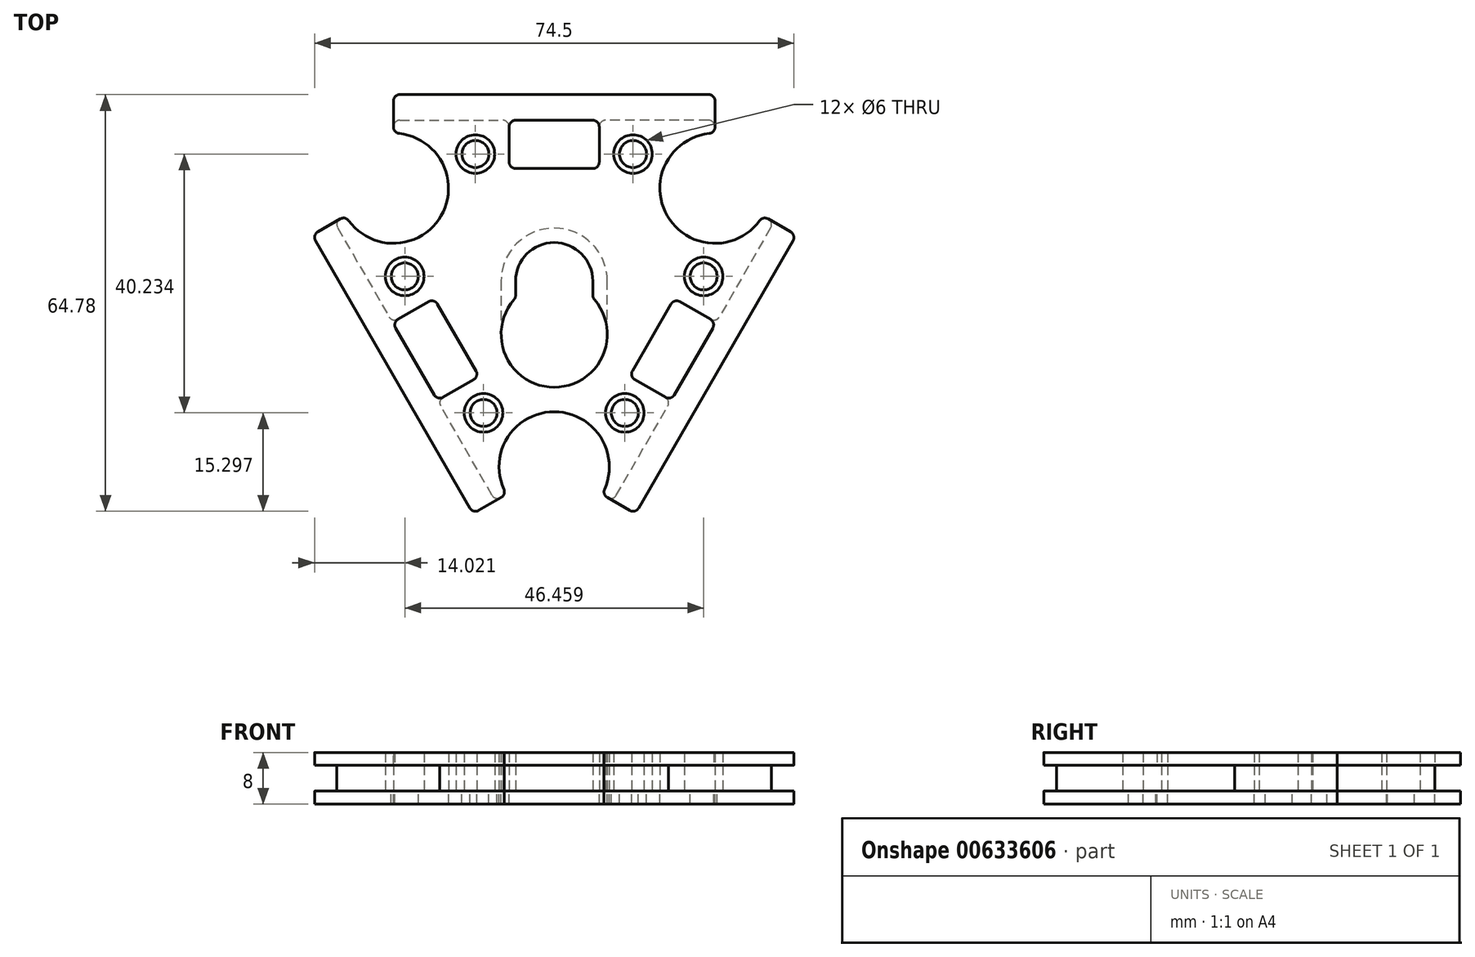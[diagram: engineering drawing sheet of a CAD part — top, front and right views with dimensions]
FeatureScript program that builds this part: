
annotation { "Feature Type Name" : "Feature", "Feature Type Description" : "" }
export const myFeature = defineFeature(function(context is Context, id is Id, definition is map)
    precondition{}
    {
        {
            var Q0;
            Q0=qCreatedBy(makeId("Top.planeOp"),FACE);
            var sketch = newSketch(context, id + "F0", { "sketchPlane" : qUnion([Q0])});
            skLineSegment(sketch, "E0.MirrorCS", {"start": v(-24, 25) * mm, "end": v(-8, 25) * mm});
            skLineSegment(sketch, "E1.MirrorCS", {"start": v(-25, 24) * mm, "end": v(-25, 23.95) * mm});
            skLineSegment(sketch, "E2.1.19", {"start": v(0, 0) * mm, "end": v(-17.58, 10.15) * mm, "construction": true});
            skArc(sketch, "E3", {"start": v(-17.58, 10.15) * mm, "mid": v(-17.37, 18.32) * mm, "end": v(-24.1, 22.95) * mm});
            skLineSegment(sketch, "E4", {"start": v(-25, 23) * mm, "end": v(0, 23) * mm, "construction": true});
            skLineSegment(sketch, "E5.top", {"start": v(0, 17.5) * mm, "end": v(-6, 17.5) * mm});
            skLineSegment(sketch, "E5.right", {"start": v(-7, 24) * mm, "end": v(-7, 18.5) * mm});
            skArc(sketch, "E6", {"start": v(6, 0) * mm, "mid": v(0, 6) * mm, "end": v(-6, 0) * mm});
            skArc(sketch, "E7", {"start": v(-6.24, -2.86) * mm, "mid": v(0, -16.5) * mm, "end": v(6.24, -2.86) * mm});
            skLineSegment(sketch, "E8", {"start": v(0, 27) * mm, "end": v(-25, 27) * mm, "construction": true});
            skCircle(sketch, "E9", {"center": v(-25, 27) * mm, "radius": 2 * mm, "construction": true});
            skLineSegment(sketch, "E10", {"start": v(-17.58, 10.15) * mm, "end": v(-7.85, 27) * mm, "construction": true});
            skLineSegment(sketch, "E11", {"start": v(-6, 0) * mm, "end": v(-6, -2.2) * mm});
            skLineSegment(sketch, "E12", {"start": v(6, -2.2) * mm, "end": v(6, 0) * mm});
            skCircle(sketch, "E13", {"center": v(-12.25, 19.75) * mm, "radius": 3 * mm});
            skCircle(sketch, "E14", {"center": v(-12.25, 19.75) * mm, "radius": 5.25 * mm, "construction": true});
            skPoint(sketch, "E15.visualSharp", {"position": v(-7, 25) * mm});
            skArc(sketch, "E15.filletArc", {"start": v(-7, 24) * mm, "mid": v(-7.3, 24.7) * mm, "end": v(-8, 25) * mm});
            skPoint(sketch, "E16.visualSharp", {"position": v(-25, 25) * mm});
            skArc(sketch, "E16.filletArc", {"start": v(-24, 25) * mm, "mid": v(-24.7, 24.7) * mm, "end": v(-25, 24) * mm});
            skPoint(sketch, "E17.visualSharp", {"position": v(-25, 23) * mm});
            skArc(sketch, "E17.filletArc", {"start": v(-25, 23.95) * mm, "mid": v(-24.74, 23.28) * mm, "end": v(-24.1, 22.95) * mm});
            skPoint(sketch, "E18.visualSharp", {"position": v(-7, 17.5) * mm});
            skArc(sketch, "E18.filletArc", {"start": v(-7, 18.5) * mm, "mid": v(-6.7, 17.8) * mm, "end": v(-6, 17.5) * mm});
            skPoint(sketch, "E19.visualSharp", {"position": v(-6, -2.59) * mm});
            skArc(sketch, "E19.filletArc", {"start": v(-6.24, -2.86) * mm, "mid": v(-6.06, -2.55) * mm, "end": v(-6, -2.2) * mm});
            skPoint(sketch, "E20.visualSharp", {"position": v(6, -2.59) * mm});
            skArc(sketch, "E20.filletArc", {"start": v(6, -2.2) * mm, "mid": v(6.06, -2.55) * mm, "end": v(6.24, -2.86) * mm});
            skLineSegment(sketch, "E21", {"start": v(0, 27) * mm, "end": v(0, 0) * mm, "construction": true});
            skLineSegment(sketch, "E22.MirrorCS", {"start": v(25, 24) * mm, "end": v(25, 23.95) * mm});
            skArc(sketch, "E23.MirrorCS", {"start": v(7, 24) * mm, "mid": v(7.3, 24.7) * mm, "end": v(8, 25) * mm});
            skArc(sketch, "E24.MirrorCS", {"start": v(24, 25) * mm, "mid": v(24.7, 24.7) * mm, "end": v(25, 24) * mm});
            skArc(sketch, "E25.MirrorCS", {"start": v(25, 23.95) * mm, "mid": v(24.74, 23.28) * mm, "end": v(24.1, 22.95) * mm});
            skArc(sketch, "E26.MirrorCS", {"start": v(7, 18.5) * mm, "mid": v(6.7, 17.8) * mm, "end": v(6, 17.5) * mm});
            skLineSegment(sketch, "E27.MirrorCS", {"start": v(25, 23) * mm, "end": v(0, 23) * mm, "construction": true});
            skLineSegment(sketch, "E28.MirrorCS", {"start": v(7, 24) * mm, "end": v(7, 18.5) * mm});
            skArc(sketch, "E29.MirrorCS", {"start": v(17.58, 10.15) * mm, "mid": v(17.37, 18.32) * mm, "end": v(24.1, 22.95) * mm});
            skPoint(sketch, "E30.MirrorP", {"position": v(25, 23) * mm});
            skPoint(sketch, "E31.MirrorP", {"position": v(25, 25) * mm});
            skPoint(sketch, "E32.MirrorP", {"position": v(7, 17.5) * mm});
            skCircle(sketch, "E33.MirrorC", {"center": v(12.25, 19.75) * mm, "radius": 5.25 * mm, "construction": true});
            skLineSegment(sketch, "E34.MirrorCS", {"start": v(24, 25) * mm, "end": v(8, 25) * mm});
            skLineSegment(sketch, "E35.MirrorCS", {"start": v(17.58, 10.15) * mm, "end": v(7.85, 27) * mm, "construction": true});
            skPoint(sketch, "E36.MirrorP", {"position": v(7, 25) * mm});
            skCircle(sketch, "E37.MirrorC", {"center": v(12.25, 19.75) * mm, "radius": 3 * mm});
            skLineSegment(sketch, "E38.MirrorCS", {"start": v(0, 17.5) * mm, "end": v(6, 17.5) * mm});
            skLineSegment(sketch, "E39.1.1", {"start": v(-15.16, -8.75) * mm, "end": v(-18.16, -3.55) * mm});
            skLineSegment(sketch, "E39.1.2", {"start": v(-33.65, 8.28) * mm, "end": v(-25.65, -5.57) * mm});
            skLineSegment(sketch, "E39.1.3", {"start": v(-15.16, -8.75) * mm, "end": v(-12.16, -13.95) * mm});
            skPoint(sketch, "E39.1.4", {"position": v(-32.42, 10.15) * mm});
            skArc(sketch, "E39.1.5", {"start": v(0, -20.3) * mm, "mid": v(-7.18, -24.2) * mm, "end": v(-7.83, -32.35) * mm});
            skPoint(sketch, "E39.1.6", {"position": v(-9.15, -34.15) * mm});
            skPoint(sketch, "E39.1.7", {"position": v(-18.66, -2.69) * mm});
            skLineSegment(sketch, "E39.1.8", {"start": v(-24.28, -5.94) * mm, "end": v(-19.52, -3.19) * mm});
            skLineSegment(sketch, "E39.1.9", {"start": v(-17.28, -18.06) * mm, "end": v(-12.52, -15.31) * mm});
            skPoint(sketch, "E39.1.10", {"position": v(-7.42, -33.15) * mm});
            skPoint(sketch, "E39.1.12", {"position": v(-34.15, 9.15) * mm});
            skArc(sketch, "E39.1.13", {"start": v(-17.58, 10.15) * mm, "mid": v(-24.55, 5.88) * mm, "end": v(-31.93, 9.4) * mm});
            skCircle(sketch, "E39.1.14", {"center": v(-10.98, -20.48) * mm, "radius": 3 * mm});
            skLineSegment(sketch, "E39.1.15", {"start": v(-9.65, -33.28) * mm, "end": v(-17.65, -19.43) * mm});
            skPoint(sketch, "E39.1.16", {"position": v(-25.15, -6.44) * mm});
            skCircle(sketch, "E39.1.17", {"center": v(-23.23, 0.73) * mm, "radius": 5.25 * mm, "construction": true});
            skPoint(sketch, "E39.1.18", {"position": v(-11.66, -14.81) * mm});
            skPoint(sketch, "E39.1.19", {"position": v(-18.15, -18.56) * mm});
            skCircle(sketch, "E39.1.20", {"center": v(-10.98, -20.48) * mm, "radius": 5.25 * mm, "construction": true});
            skCircle(sketch, "E39.1.21", {"center": v(-23.23, 0.73) * mm, "radius": 3 * mm});
            skArc(sketch, "E39.1.22", {"start": v(-17.28, -18.06) * mm, "mid": v(-17.75, -18.67) * mm, "end": v(-17.65, -19.43) * mm});
            skArc(sketch, "E39.1.23", {"start": v(-24.28, -5.94) * mm, "mid": v(-25.04, -6.04) * mm, "end": v(-25.65, -5.57) * mm});
            skArc(sketch, "E39.1.24", {"start": v(-19.52, -3.19) * mm, "mid": v(-18.76, -3.09) * mm, "end": v(-18.16, -3.55) * mm});
            skArc(sketch, "E39.1.25", {"start": v(-12.52, -15.31) * mm, "mid": v(-12.06, -14.7) * mm, "end": v(-12.16, -13.95) * mm});
            skArc(sketch, "E39.1.26", {"start": v(-33.24, 9.68) * mm, "mid": v(-32.53, 9.79) * mm, "end": v(-31.93, 9.4) * mm});
            skArc(sketch, "E39.1.27", {"start": v(-33.65, 8.28) * mm, "mid": v(-33.75, 9.04) * mm, "end": v(-33.28, 9.65) * mm});
            skArc(sketch, "E39.1.28", {"start": v(-8.24, -33.62) * mm, "mid": v(-7.79, -33.07) * mm, "end": v(-7.83, -32.35) * mm});
            skArc(sketch, "E39.1.29", {"start": v(-9.65, -33.28) * mm, "mid": v(-9.04, -33.75) * mm, "end": v(-8.28, -33.65) * mm});
            skLineSegment(sketch, "E39.1.30", {"start": v(-8.28, -33.65) * mm, "end": v(-8.24, -33.62) * mm});
            skLineSegment(sketch, "E39.1.31", {"start": v(-33.28, 9.65) * mm, "end": v(-33.24, 9.68) * mm});
            skLineSegment(sketch, "E39.2.1", {"start": v(15.16, -8.75) * mm, "end": v(12.16, -13.95) * mm});
            skLineSegment(sketch, "E39.2.2", {"start": v(9.65, -33.28) * mm, "end": v(17.65, -19.43) * mm});
            skLineSegment(sketch, "E39.2.3", {"start": v(15.16, -8.75) * mm, "end": v(18.16, -3.55) * mm});
            skPoint(sketch, "E39.2.4", {"position": v(7.42, -33.15) * mm});
            skArc(sketch, "E39.2.5", {"start": v(17.58, 10.15) * mm, "mid": v(24.55, 5.88) * mm, "end": v(31.93, 9.4) * mm});
            skPoint(sketch, "E39.2.6", {"position": v(34.15, 9.15) * mm});
            skPoint(sketch, "E39.2.7", {"position": v(11.66, -14.81) * mm});
            skLineSegment(sketch, "E39.2.8", {"start": v(17.28, -18.06) * mm, "end": v(12.52, -15.31) * mm});
            skLineSegment(sketch, "E39.2.9", {"start": v(24.28, -5.94) * mm, "end": v(19.52, -3.19) * mm});
            skPoint(sketch, "E39.2.10", {"position": v(32.42, 10.15) * mm});
            skPoint(sketch, "E39.2.12", {"position": v(9.15, -34.15) * mm});
            skArc(sketch, "E39.2.13", {"start": v(0, -20.3) * mm, "mid": v(7.18, -24.2) * mm, "end": v(7.83, -32.35) * mm});
            skCircle(sketch, "E39.2.14", {"center": v(23.23, 0.73) * mm, "radius": 3 * mm});
            skLineSegment(sketch, "E39.2.15", {"start": v(33.65, 8.28) * mm, "end": v(25.65, -5.57) * mm});
            skPoint(sketch, "E39.2.16", {"position": v(18.15, -18.56) * mm});
            skCircle(sketch, "E39.2.17", {"center": v(10.98, -20.48) * mm, "radius": 5.25 * mm, "construction": true});
            skPoint(sketch, "E39.2.18", {"position": v(18.66, -2.69) * mm});
            skPoint(sketch, "E39.2.19", {"position": v(25.15, -6.44) * mm});
            skCircle(sketch, "E39.2.20", {"center": v(23.23, 0.73) * mm, "radius": 5.25 * mm, "construction": true});
            skCircle(sketch, "E39.2.21", {"center": v(10.98, -20.48) * mm, "radius": 3 * mm});
            skArc(sketch, "E39.2.22", {"start": v(24.28, -5.94) * mm, "mid": v(25.04, -6.04) * mm, "end": v(25.65, -5.57) * mm});
            skArc(sketch, "E39.2.23", {"start": v(17.28, -18.06) * mm, "mid": v(17.75, -18.67) * mm, "end": v(17.65, -19.43) * mm});
            skArc(sketch, "E39.2.24", {"start": v(12.52, -15.31) * mm, "mid": v(12.06, -14.7) * mm, "end": v(12.16, -13.95) * mm});
            skArc(sketch, "E39.2.25", {"start": v(19.52, -3.19) * mm, "mid": v(18.76, -3.09) * mm, "end": v(18.16, -3.55) * mm});
            skArc(sketch, "E39.2.26", {"start": v(8.24, -33.62) * mm, "mid": v(7.79, -33.07) * mm, "end": v(7.83, -32.35) * mm});
            skArc(sketch, "E39.2.27", {"start": v(9.65, -33.28) * mm, "mid": v(9.04, -33.75) * mm, "end": v(8.28, -33.65) * mm});
            skArc(sketch, "E39.2.28", {"start": v(33.24, 9.68) * mm, "mid": v(32.53, 9.79) * mm, "end": v(31.93, 9.4) * mm});
            skArc(sketch, "E39.2.29", {"start": v(33.65, 8.28) * mm, "mid": v(33.75, 9.04) * mm, "end": v(33.28, 9.65) * mm});
            skLineSegment(sketch, "E39.2.30", {"start": v(33.28, 9.65) * mm, "end": v(33.24, 9.68) * mm});
            skLineSegment(sketch, "E39.2.31", {"start": v(8.28, -33.65) * mm, "end": v(8.24, -33.62) * mm});
            skSolve(sketch);
        }
        {
            var Q0;
            Q0=qSketchRegion(id+"F0",true);
            extrude(context, id + "F1", {"entities" : qUnion([Q0]), "depth" : 4 * mm, "offsetDistance" : 25 * mm});
        }
        {
            var Q0;
            Q0=makeQuery(id+"F1.opExtrude","CAP_FACE",FACE,{"disambiguationData":[OSD([sQuery(id+"F0.wireOp",EDGE,"E0.MirrorCS"),sQuery(id+"F0.wireOp",EDGE,"E1.MirrorCS"),sQuery(id+"F0.wireOp",EDGE,"E3"),sQuery(id+"F0.wireOp",EDGE,"E5.top"),sQuery(id+"F0.wireOp",EDGE,"E5.right"),sQuery(id+"F0.wireOp",EDGE,"E6"),sQuery(id+"F0.wireOp",EDGE,"E7"),sQuery(id+"F0.wireOp",EDGE,"E11"),sQuery(id+"F0.wireOp",EDGE,"E12"),sQuery(id+"F0.wireOp",EDGE,"E13"),sQuery(id+"F0.wireOp",EDGE,"E15.filletArc"),sQuery(id+"F0.wireOp",EDGE,"E16.filletArc"),sQuery(id+"F0.wireOp",EDGE,"E17.filletArc"),sQuery(id+"F0.wireOp",EDGE,"E18.filletArc"),sQuery(id+"F0.wireOp",EDGE,"E19.filletArc"),sQuery(id+"F0.wireOp",EDGE,"E20.filletArc"),sQuery(id+"F0.wireOp",EDGE,"E22.MirrorCS"),sQuery(id+"F0.wireOp",EDGE,"E23.MirrorCS"),sQuery(id+"F0.wireOp",EDGE,"E24.MirrorCS"),sQuery(id+"F0.wireOp",EDGE,"E25.MirrorCS"),sQuery(id+"F0.wireOp",EDGE,"E26.MirrorCS"),sQuery(id+"F0.wireOp",EDGE,"E28.MirrorCS"),sQuery(id+"F0.wireOp",EDGE,"E29.MirrorCS"),sQuery(id+"F0.wireOp",EDGE,"E34.MirrorCS"),sQuery(id+"F0.wireOp",EDGE,"E37.MirrorC"),sQuery(id+"F0.wireOp",EDGE,"E38.MirrorCS"),sQuery(id+"F0.wireOp",EDGE,"E39.1.1"),sQuery(id+"F0.wireOp",EDGE,"E39.1.2"),sQuery(id+"F0.wireOp",EDGE,"E39.1.3"),sQuery(id+"F0.wireOp",EDGE,"E39.1.5"),sQuery(id+"F0.wireOp",EDGE,"E39.1.8"),sQuery(id+"F0.wireOp",EDGE,"E39.1.9"),sQuery(id+"F0.wireOp",EDGE,"E39.1.13"),sQuery(id+"F0.wireOp",EDGE,"E39.1.14"),sQuery(id+"F0.wireOp",EDGE,"E39.1.15"),sQuery(id+"F0.wireOp",EDGE,"E39.1.21"),sQuery(id+"F0.wireOp",EDGE,"E39.1.22"),sQuery(id+"F0.wireOp",EDGE,"E39.1.23"),sQuery(id+"F0.wireOp",EDGE,"E39.1.24"),sQuery(id+"F0.wireOp",EDGE,"E39.1.25"),sQuery(id+"F0.wireOp",EDGE,"E39.1.26"),sQuery(id+"F0.wireOp",EDGE,"E39.1.27"),sQuery(id+"F0.wireOp",EDGE,"E39.1.28"),sQuery(id+"F0.wireOp",EDGE,"E39.1.29"),sQuery(id+"F0.wireOp",EDGE,"E39.1.30"),sQuery(id+"F0.wireOp",EDGE,"E39.1.31"),sQuery(id+"F0.wireOp",EDGE,"E39.2.1"),sQuery(id+"F0.wireOp",EDGE,"E39.2.2"),sQuery(id+"F0.wireOp",EDGE,"E39.2.3"),sQuery(id+"F0.wireOp",EDGE,"E39.2.5"),sQuery(id+"F0.wireOp",EDGE,"E39.2.8"),sQuery(id+"F0.wireOp",EDGE,"E39.2.9"),sQuery(id+"F0.wireOp",EDGE,"E39.2.13"),sQuery(id+"F0.wireOp",EDGE,"E39.2.14"),sQuery(id+"F0.wireOp",EDGE,"E39.2.15"),sQuery(id+"F0.wireOp",EDGE,"E39.2.21"),sQuery(id+"F0.wireOp",EDGE,"E39.2.22"),sQuery(id+"F0.wireOp",EDGE,"E39.2.23"),sQuery(id+"F0.wireOp",EDGE,"E39.2.24"),sQuery(id+"F0.wireOp",EDGE,"E39.2.25"),sQuery(id+"F0.wireOp",EDGE,"E39.2.26"),sQuery(id+"F0.wireOp",EDGE,"E39.2.27"),sQuery(id+"F0.wireOp",EDGE,"E39.2.28"),sQuery(id+"F0.wireOp",EDGE,"E39.2.29"),sQuery(id+"F0.wireOp",EDGE,"E39.2.30"),sQuery(id+"F0.wireOp",EDGE,"E39.2.31")])],"isStart":false});
            var sketch = newSketch(context, id + "F2", { "sketchPlane" : qUnion([Q0])});
            skLineSegment(sketch, "E40.1.19", {"start": v(0, 0) * mm, "end": v(-17.58, 10.15) * mm, "construction": true});
            skArc(sketch, "E41", {"start": v(-17.58, 10.15) * mm, "mid": v(-17.37, 18.32) * mm, "end": v(-24.1, 22.95) * mm});
            skLineSegment(sketch, "E42", {"start": v(-25, 23) * mm, "end": v(0, 23) * mm, "construction": true});
            skArc(sketch, "E43", {"start": v(6, 0) * mm, "mid": v(0, 6) * mm, "end": v(-6, 0) * mm});
            skArc(sketch, "E44", {"start": v(-6.24, -2.86) * mm, "mid": v(0, -16.5) * mm, "end": v(6.24, -2.86) * mm});
            skLineSegment(sketch, "E45", {"start": v(0, 27) * mm, "end": v(-25, 27) * mm, "construction": true});
            skCircle(sketch, "E46", {"center": v(-25, 27) * mm, "radius": 2 * mm, "construction": true});
            skLineSegment(sketch, "E47", {"start": v(-17.58, 10.15) * mm, "end": v(-7.85, 27) * mm, "construction": true});
            skLineSegment(sketch, "E48", {"start": v(-6, 0) * mm, "end": v(-6, -2.2) * mm});
            skLineSegment(sketch, "E49", {"start": v(6, -2.2) * mm, "end": v(6, 0) * mm});
            skCircle(sketch, "E50", {"center": v(-12.25, 19.75) * mm, "radius": 2.1 * mm});
            skCircle(sketch, "E51", {"center": v(-12.25, 19.75) * mm, "radius": 5.25 * mm, "construction": true});
            skPoint(sketch, "E52.visualSharp", {"position": v(-25, 25) * mm});
            skPoint(sketch, "E53.visualSharp", {"position": v(-25, 23) * mm});
            skArc(sketch, "E53.filletArc", {"start": v(-25, 23.95) * mm, "mid": v(-24.74, 23.28) * mm, "end": v(-24.1, 22.95) * mm});
            skPoint(sketch, "E54.visualSharp", {"position": v(-6, -2.59) * mm});
            skArc(sketch, "E54.filletArc", {"start": v(-6.24, -2.86) * mm, "mid": v(-6.06, -2.55) * mm, "end": v(-6, -2.2) * mm});
            skPoint(sketch, "E55.visualSharp", {"position": v(6, -2.59) * mm});
            skArc(sketch, "E55.filletArc", {"start": v(6, -2.2) * mm, "mid": v(6.06, -2.55) * mm, "end": v(6.24, -2.86) * mm});
            skLineSegment(sketch, "E56", {"start": v(0, 27) * mm, "end": v(0, 0) * mm, "construction": true});
            skLineSegment(sketch, "E57", {"start": v(0, 29) * mm, "end": v(-24, 29) * mm});
            skLineSegment(sketch, "E58", {"start": v(-25, 28) * mm, "end": v(-25, 23.95) * mm});
            skPoint(sketch, "E59.visualSharp", {"position": v(-25, 29) * mm});
            skArc(sketch, "E59.filletArc", {"start": v(-24, 29) * mm, "mid": v(-24.7, 28.7) * mm, "end": v(-25, 28) * mm});
            skLineSegment(sketch, "E60", {"start": v(-25, 25) * mm, "end": v(0, 25) * mm, "construction": true});
            skLineSegment(sketch, "E61", {"start": v(0, 25) * mm, "end": v(-6, 25) * mm});
            skLineSegment(sketch, "E62", {"start": v(-7, 24) * mm, "end": v(-7, 18.5) * mm});
            skLineSegment(sketch, "E63", {"start": v(-6, 17.5) * mm, "end": v(0, 17.5) * mm});
            skPoint(sketch, "E64.visualSharp", {"position": v(-7, 17.5) * mm});
            skArc(sketch, "E64.filletArc", {"start": v(-7, 18.5) * mm, "mid": v(-6.7, 17.8) * mm, "end": v(-6, 17.5) * mm});
            skPoint(sketch, "E65.visualSharp", {"position": v(-7, 25) * mm});
            skArc(sketch, "E65.filletArc", {"start": v(-6, 25) * mm, "mid": v(-6.7, 24.7) * mm, "end": v(-7, 24) * mm});
            skArc(sketch, "E66.MirrorCS", {"start": v(25, 23.95) * mm, "mid": v(24.74, 23.28) * mm, "end": v(24.1, 22.95) * mm});
            skArc(sketch, "E67.MirrorCS", {"start": v(6, 25) * mm, "mid": v(6.7, 24.7) * mm, "end": v(7, 24) * mm});
            skArc(sketch, "E68.MirrorCS", {"start": v(7, 18.5) * mm, "mid": v(6.7, 17.8) * mm, "end": v(6, 17.5) * mm});
            skArc(sketch, "E69.MirrorCS", {"start": v(24, 29) * mm, "mid": v(24.7, 28.7) * mm, "end": v(25, 28) * mm});
            skLineSegment(sketch, "E70.MirrorCS", {"start": v(0, 25) * mm, "end": v(6, 25) * mm});
            skPoint(sketch, "E71.MirrorP", {"position": v(25, 29) * mm});
            skPoint(sketch, "E72.MirrorP", {"position": v(25, 23) * mm});
            skCircle(sketch, "E73.MirrorC", {"center": v(12.25, 19.75) * mm, "radius": 2.1 * mm});
            skLineSegment(sketch, "E74.MirrorCS", {"start": v(6, 17.5) * mm, "end": v(0, 17.5) * mm});
            skLineSegment(sketch, "E75.MirrorCS", {"start": v(0, 29) * mm, "end": v(24, 29) * mm});
            skPoint(sketch, "E76.MirrorP", {"position": v(25, 25) * mm});
            skPoint(sketch, "E77.MirrorP", {"position": v(7, 25) * mm});
            skArc(sketch, "E78.MirrorCS", {"start": v(17.58, 10.15) * mm, "mid": v(17.37, 18.32) * mm, "end": v(24.1, 22.95) * mm});
            skCircle(sketch, "E79.MirrorC", {"center": v(25, 27) * mm, "radius": 2 * mm, "construction": true});
            skLineSegment(sketch, "E80.MirrorCS", {"start": v(17.58, 10.15) * mm, "end": v(7.85, 27) * mm, "construction": true});
            skPoint(sketch, "E81.MirrorP", {"position": v(7, 17.5) * mm});
            skLineSegment(sketch, "E82.MirrorCS", {"start": v(25, 25) * mm, "end": v(0, 25) * mm, "construction": true});
            skLineSegment(sketch, "E83.MirrorCS", {"start": v(25, 23) * mm, "end": v(0, 23) * mm, "construction": true});
            skLineSegment(sketch, "E84.MirrorCS", {"start": v(0, 27) * mm, "end": v(25, 27) * mm, "construction": true});
            skLineSegment(sketch, "E85.MirrorCS", {"start": v(25, 28) * mm, "end": v(25, 23.95) * mm});
            skLineSegment(sketch, "E86.MirrorCS", {"start": v(7, 24) * mm, "end": v(7, 18.5) * mm});
            skCircle(sketch, "E87.MirrorC", {"center": v(12.25, 19.75) * mm, "radius": 5.25 * mm, "construction": true});
            skLineSegment(sketch, "E88.1.0", {"start": v(-25.11, -14.5) * mm, "end": v(-13.11, -35.28) * mm});
            skLineSegment(sketch, "E88.1.1", {"start": v(-12.16, -13.95) * mm, "end": v(-15.16, -8.75) * mm});
            skLineSegment(sketch, "E88.1.2", {"start": v(-9.15, -34.15) * mm, "end": v(-21.65, -12.5) * mm, "construction": true});
            skPoint(sketch, "E88.1.3", {"position": v(-12.61, -36.15) * mm});
            skPoint(sketch, "E88.1.4", {"position": v(-9.15, -34.15) * mm});
            skLineSegment(sketch, "E88.1.5", {"start": v(-23.38, -13.5) * mm, "end": v(-35.88, 8.15) * mm, "construction": true});
            skPoint(sketch, "E88.1.6", {"position": v(-34.15, 9.15) * mm});
            skLineSegment(sketch, "E88.1.7", {"start": v(-24.28, -5.94) * mm, "end": v(-19.52, -3.19) * mm});
            skCircle(sketch, "E88.1.8", {"center": v(-10.88, -35.15) * mm, "radius": 2 * mm, "construction": true});
            skArc(sketch, "E88.1.9", {"start": v(0, -20.3) * mm, "mid": v(-7.18, -24.2) * mm, "end": v(-7.83, -32.35) * mm});
            skLineSegment(sketch, "E88.1.10", {"start": v(-23.38, -13.5) * mm, "end": v(-10.88, -35.15) * mm, "construction": true});
            skPoint(sketch, "E88.1.11", {"position": v(-25.15, -6.44) * mm});
            skPoint(sketch, "E88.1.12", {"position": v(-7.42, -33.15) * mm});
            skPoint(sketch, "E88.1.13", {"position": v(-18.66, -2.69) * mm});
            skPoint(sketch, "E88.1.14", {"position": v(-37.61, 7.15) * mm});
            skLineSegment(sketch, "E88.1.15", {"start": v(-32.42, 10.15) * mm, "end": v(-19.92, -11.5) * mm, "construction": true});
            skCircle(sketch, "E88.1.16", {"center": v(-10.98, -20.48) * mm, "radius": 5.25 * mm, "construction": true});
            skCircle(sketch, "E88.1.17", {"center": v(-35.88, 8.15) * mm, "radius": 2 * mm, "construction": true});
            skCircle(sketch, "E88.1.18", {"center": v(-23.23, 0.73) * mm, "radius": 2.1 * mm});
            skPoint(sketch, "E88.1.19", {"position": v(-18.15, -18.56) * mm});
            skLineSegment(sketch, "E88.1.20", {"start": v(-17.58, 10.15) * mm, "end": v(-27.3, -6.7) * mm, "construction": true});
            skLineSegment(sketch, "E88.1.21", {"start": v(0, -20.3) * mm, "end": v(-19.46, -20.3) * mm, "construction": true});
            skLineSegment(sketch, "E88.1.22", {"start": v(-18.16, -3.55) * mm, "end": v(-15.16, -8.75) * mm});
            skPoint(sketch, "E88.1.23", {"position": v(-11.66, -14.81) * mm});
            skArc(sketch, "E88.1.24", {"start": v(-17.58, 10.15) * mm, "mid": v(-24.55, 5.88) * mm, "end": v(-31.93, 9.4) * mm});
            skLineSegment(sketch, "E88.1.25", {"start": v(-25.11, -14.5) * mm, "end": v(-37.11, 6.28) * mm});
            skPoint(sketch, "E88.1.26", {"position": v(-32.42, 10.15) * mm});
            skLineSegment(sketch, "E88.1.27", {"start": v(-34.15, 9.15) * mm, "end": v(-21.65, -12.5) * mm, "construction": true});
            skCircle(sketch, "E88.1.28", {"center": v(-23.23, 0.73) * mm, "radius": 5.25 * mm, "construction": true});
            skCircle(sketch, "E88.1.29", {"center": v(-10.98, -20.48) * mm, "radius": 2.1 * mm});
            skLineSegment(sketch, "E88.1.30", {"start": v(-7.42, -33.15) * mm, "end": v(-19.92, -11.5) * mm, "construction": true});
            skLineSegment(sketch, "E88.1.31", {"start": v(-21.65, -12.5) * mm, "end": v(-18.65, -17.7) * mm});
            skLineSegment(sketch, "E88.1.32", {"start": v(-21.65, -12.5) * mm, "end": v(-24.65, -7.3) * mm});
            skLineSegment(sketch, "E88.1.33", {"start": v(-17.28, -18.06) * mm, "end": v(-12.52, -15.31) * mm});
            skArc(sketch, "E88.1.34", {"start": v(-8.24, -33.62) * mm, "mid": v(-7.79, -33.07) * mm, "end": v(-7.83, -32.35) * mm});
            skArc(sketch, "E88.1.35", {"start": v(-19.52, -3.19) * mm, "mid": v(-18.76, -3.09) * mm, "end": v(-18.16, -3.55) * mm});
            skArc(sketch, "E88.1.36", {"start": v(-24.65, -7.3) * mm, "mid": v(-24.75, -6.55) * mm, "end": v(-24.28, -5.94) * mm});
            skArc(sketch, "E88.1.37", {"start": v(-33.24, 9.68) * mm, "mid": v(-32.53, 9.79) * mm, "end": v(-31.93, 9.4) * mm});
            skArc(sketch, "E88.1.38", {"start": v(-18.65, -17.7) * mm, "mid": v(-18.04, -18.16) * mm, "end": v(-17.28, -18.06) * mm});
            skArc(sketch, "E88.1.39", {"start": v(-13.11, -35.28) * mm, "mid": v(-12.5, -35.75) * mm, "end": v(-11.75, -35.65) * mm});
            skLineSegment(sketch, "E88.1.40", {"start": v(-11.75, -35.65) * mm, "end": v(-8.24, -33.62) * mm});
            skLineSegment(sketch, "E88.1.41", {"start": v(-36.75, 7.65) * mm, "end": v(-33.24, 9.68) * mm});
            skArc(sketch, "E88.1.42", {"start": v(-37.11, 6.28) * mm, "mid": v(-37.21, 7.04) * mm, "end": v(-36.75, 7.65) * mm});
            skArc(sketch, "E88.1.43", {"start": v(-12.52, -15.31) * mm, "mid": v(-12.06, -14.7) * mm, "end": v(-12.16, -13.95) * mm});
            skLineSegment(sketch, "E88.2.0", {"start": v(25.11, -14.5) * mm, "end": v(37.11, 6.28) * mm});
            skLineSegment(sketch, "E88.2.1", {"start": v(18.16, -3.55) * mm, "end": v(15.16, -8.75) * mm});
            skLineSegment(sketch, "E88.2.2", {"start": v(34.15, 9.15) * mm, "end": v(21.65, -12.5) * mm, "construction": true});
            skPoint(sketch, "E88.2.3", {"position": v(37.61, 7.15) * mm});
            skPoint(sketch, "E88.2.4", {"position": v(34.15, 9.15) * mm});
            skLineSegment(sketch, "E88.2.5", {"start": v(23.38, -13.5) * mm, "end": v(10.88, -35.15) * mm, "construction": true});
            skPoint(sketch, "E88.2.6", {"position": v(9.15, -34.15) * mm});
            skLineSegment(sketch, "E88.2.7", {"start": v(17.28, -18.06) * mm, "end": v(12.52, -15.31) * mm});
            skCircle(sketch, "E88.2.8", {"center": v(35.88, 8.15) * mm, "radius": 2 * mm, "construction": true});
            skArc(sketch, "E88.2.9", {"start": v(17.58, 10.15) * mm, "mid": v(24.55, 5.88) * mm, "end": v(31.93, 9.4) * mm});
            skLineSegment(sketch, "E88.2.10", {"start": v(23.38, -13.5) * mm, "end": v(35.88, 8.15) * mm, "construction": true});
            skPoint(sketch, "E88.2.11", {"position": v(18.15, -18.56) * mm});
            skPoint(sketch, "E88.2.12", {"position": v(32.42, 10.15) * mm});
            skPoint(sketch, "E88.2.13", {"position": v(11.66, -14.81) * mm});
            skPoint(sketch, "E88.2.14", {"position": v(12.61, -36.15) * mm});
            skLineSegment(sketch, "E88.2.15", {"start": v(7.42, -33.15) * mm, "end": v(19.92, -11.5) * mm, "construction": true});
            skCircle(sketch, "E88.2.16", {"center": v(23.23, 0.73) * mm, "radius": 5.25 * mm, "construction": true});
            skCircle(sketch, "E88.2.17", {"center": v(10.88, -35.15) * mm, "radius": 2 * mm, "construction": true});
            skCircle(sketch, "E88.2.18", {"center": v(10.98, -20.48) * mm, "radius": 2.1 * mm});
            skPoint(sketch, "E88.2.19", {"position": v(25.15, -6.44) * mm});
            skLineSegment(sketch, "E88.2.20", {"start": v(0, -20.3) * mm, "end": v(19.46, -20.3) * mm, "construction": true});
            skLineSegment(sketch, "E88.2.21", {"start": v(17.58, 10.15) * mm, "end": v(27.3, -6.7) * mm, "construction": true});
            skLineSegment(sketch, "E88.2.22", {"start": v(12.16, -13.95) * mm, "end": v(15.16, -8.75) * mm});
            skPoint(sketch, "E88.2.23", {"position": v(18.66, -2.69) * mm});
            skArc(sketch, "E88.2.24", {"start": v(0, -20.3) * mm, "mid": v(7.18, -24.2) * mm, "end": v(7.83, -32.35) * mm});
            skLineSegment(sketch, "E88.2.25", {"start": v(25.11, -14.5) * mm, "end": v(13.11, -35.28) * mm});
            skPoint(sketch, "E88.2.26", {"position": v(7.42, -33.15) * mm});
            skLineSegment(sketch, "E88.2.27", {"start": v(9.15, -34.15) * mm, "end": v(21.65, -12.5) * mm, "construction": true});
            skCircle(sketch, "E88.2.28", {"center": v(10.98, -20.48) * mm, "radius": 5.25 * mm, "construction": true});
            skCircle(sketch, "E88.2.29", {"center": v(23.23, 0.73) * mm, "radius": 2.1 * mm});
            skLineSegment(sketch, "E88.2.30", {"start": v(32.42, 10.15) * mm, "end": v(19.92, -11.5) * mm, "construction": true});
            skLineSegment(sketch, "E88.2.31", {"start": v(21.65, -12.5) * mm, "end": v(24.65, -7.3) * mm});
            skLineSegment(sketch, "E88.2.32", {"start": v(21.65, -12.5) * mm, "end": v(18.65, -17.7) * mm});
            skLineSegment(sketch, "E88.2.33", {"start": v(24.28, -5.94) * mm, "end": v(19.52, -3.19) * mm});
            skArc(sketch, "E88.2.34", {"start": v(33.24, 9.68) * mm, "mid": v(32.53, 9.79) * mm, "end": v(31.93, 9.4) * mm});
            skArc(sketch, "E88.2.35", {"start": v(12.52, -15.31) * mm, "mid": v(12.06, -14.7) * mm, "end": v(12.16, -13.95) * mm});
            skArc(sketch, "E88.2.36", {"start": v(18.65, -17.7) * mm, "mid": v(18.04, -18.16) * mm, "end": v(17.28, -18.06) * mm});
            skArc(sketch, "E88.2.37", {"start": v(8.24, -33.62) * mm, "mid": v(7.79, -33.07) * mm, "end": v(7.83, -32.35) * mm});
            skArc(sketch, "E88.2.38", {"start": v(24.65, -7.3) * mm, "mid": v(24.75, -6.55) * mm, "end": v(24.28, -5.94) * mm});
            skArc(sketch, "E88.2.39", {"start": v(37.11, 6.28) * mm, "mid": v(37.21, 7.04) * mm, "end": v(36.75, 7.65) * mm});
            skLineSegment(sketch, "E88.2.40", {"start": v(36.75, 7.65) * mm, "end": v(33.24, 9.68) * mm});
            skLineSegment(sketch, "E88.2.41", {"start": v(11.75, -35.65) * mm, "end": v(8.24, -33.62) * mm});
            skArc(sketch, "E88.2.42", {"start": v(13.11, -35.28) * mm, "mid": v(12.5, -35.75) * mm, "end": v(11.75, -35.65) * mm});
            skArc(sketch, "E88.2.43", {"start": v(19.52, -3.19) * mm, "mid": v(18.76, -3.09) * mm, "end": v(18.16, -3.55) * mm});
            skSolve(sketch);
        }
        {
            var Q0;
            Q0=makeQuery(id+"F2.imprint","IMPRINT",FACE,{"disambiguationData":[TD([[makeQuery(id+"F2.imprint","IMPRINT",EDGE,{"derivedFrom":sQuery(id+"F2.wireOp",EDGE,"E43")}),-1.0]])]});
            var Q1;
            Q1=makeQuery(id+"F2.imprint","IMPRINT",FACE,{"disambiguationData":[TD([[makeQuery(id+"F2.imprint","IMPRINT",EDGE,{"derivedFrom":sQuery(id+"F2.wireOp",EDGE,"E57")}),1.0]])]});
            var Q2;
            Q2=makeQuery(id+"F2.imprint","IMPRINT",FACE,{"disambiguationData":[TD([[makeQuery(id+"F2.imprint","IMPRINT",EDGE,{"derivedFrom":sQuery(id+"F2.wireOp",EDGE,"E88.1.0")}),1.0]])]});
            var Q3;
            Q3=makeQuery(id+"F2.imprint","IMPRINT",FACE,{"disambiguationData":[TD([[makeQuery(id+"F2.imprint","IMPRINT",EDGE,{"derivedFrom":sQuery(id+"F2.wireOp",EDGE,"E88.2.0")}),1.0]])]});
            extrude(context, id + "F3", {"entities" : qUnion([Q0, Q1, Q2, Q3]), "depth" : 2 * mm, "offsetDistance" : 25 * mm});
        }
        {
            var Q0;
            Q0=qCreatedBy(makeId("Top.planeOp"),FACE);
            var sketch = newSketch(context, id + "F4", { "sketchPlane" : qUnion([Q0])});
            skLineSegment(sketch, "E89.1.19", {"start": v(0, 0) * mm, "end": v(-17.58, 10.15) * mm, "construction": true});
            skArc(sketch, "E90", {"start": v(-17.58, 10.15) * mm, "mid": v(-17.37, 18.32) * mm, "end": v(-24.1, 22.95) * mm});
            skLineSegment(sketch, "E91", {"start": v(-25, 23) * mm, "end": v(0, 23) * mm, "construction": true});
            skArc(sketch, "E92", {"start": v(8.25, 0) * mm, "mid": v(0, 8.25) * mm, "end": v(-8.25, 0) * mm});
            skArc(sketch, "E93", {"start": v(-8.25, -8.25) * mm, "mid": v(0, -16.5) * mm, "end": v(8.25, -8.25) * mm});
            skLineSegment(sketch, "E94", {"start": v(0, 27) * mm, "end": v(-25, 27) * mm, "construction": true});
            skCircle(sketch, "E95", {"center": v(-25, 27) * mm, "radius": 2 * mm, "construction": true});
            skLineSegment(sketch, "E96", {"start": v(-17.58, 10.15) * mm, "end": v(-7.85, 27) * mm, "construction": true});
            skLineSegment(sketch, "E97", {"start": v(-8.25, 0) * mm, "end": v(-8.25, -8.25) * mm});
            skLineSegment(sketch, "E98", {"start": v(8.25, -8.25) * mm, "end": v(8.25, 0) * mm});
            skCircle(sketch, "E99", {"center": v(-12.25, 19.75) * mm, "radius": 2.1 * mm});
            skCircle(sketch, "E100", {"center": v(-12.25, 19.75) * mm, "radius": 5.25 * mm, "construction": true});
            skPoint(sketch, "E101.visualSharp", {"position": v(-8.25, -8.25) * mm});
            skLineSegment(sketch, "E101.filletArc", {"start": v(-8.25, -8.25) * mm, "end": v(-8.25, -8.25) * mm});
            skPoint(sketch, "E102.visualSharp", {"position": v(8.25, -8.25) * mm});
            skLineSegment(sketch, "E102.filletArc", {"start": v(8.25, -8.25) * mm, "end": v(8.25, -8.25) * mm});
            skLineSegment(sketch, "E103", {"start": v(0, 27) * mm, "end": v(0, 0) * mm, "construction": true});
            skLineSegment(sketch, "E104", {"start": v(0, 29) * mm, "end": v(-24, 29) * mm});
            skLineSegment(sketch, "E105", {"start": v(-25, 25) * mm, "end": v(0, 25) * mm, "construction": true});
            skLineSegment(sketch, "E106", {"start": v(0, 25) * mm, "end": v(-6, 25) * mm});
            skLineSegment(sketch, "E107", {"start": v(-7, 24) * mm, "end": v(-7, 18.5) * mm});
            skLineSegment(sketch, "E108", {"start": v(-6, 17.5) * mm, "end": v(0, 17.5) * mm});
            skPoint(sketch, "E109.visualSharp", {"position": v(-7, 17.5) * mm});
            skArc(sketch, "E109.filletArc", {"start": v(-7, 18.5) * mm, "mid": v(-6.7, 17.8) * mm, "end": v(-6, 17.5) * mm});
            skPoint(sketch, "E110.visualSharp", {"position": v(-7, 25) * mm});
            skArc(sketch, "E110.filletArc", {"start": v(-6, 25) * mm, "mid": v(-6.7, 24.7) * mm, "end": v(-7, 24) * mm});
            skLineSegment(sketch, "E111", {"start": v(-25, 28) * mm, "end": v(-25, 23.95) * mm});
            skPoint(sketch, "E112.visualSharp", {"position": v(-25, 29) * mm});
            skArc(sketch, "E112.filletArc", {"start": v(-24, 29) * mm, "mid": v(-24.7, 28.7) * mm, "end": v(-25, 28) * mm});
            skPoint(sketch, "E113.visualSharp", {"position": v(-25, 23) * mm});
            skArc(sketch, "E113.filletArc", {"start": v(-25, 23.95) * mm, "mid": v(-24.74, 23.28) * mm, "end": v(-24.1, 22.95) * mm});
            skArc(sketch, "E114.MirrorCS", {"start": v(24, 29) * mm, "mid": v(24.7, 28.7) * mm, "end": v(25, 28) * mm});
            skArc(sketch, "E115.MirrorCS", {"start": v(6, 25) * mm, "mid": v(6.7, 24.7) * mm, "end": v(7, 24) * mm});
            skArc(sketch, "E116.MirrorCS", {"start": v(25, 23.95) * mm, "mid": v(24.74, 23.28) * mm, "end": v(24.1, 22.95) * mm});
            skArc(sketch, "E117.MirrorCS", {"start": v(7, 18.5) * mm, "mid": v(6.7, 17.8) * mm, "end": v(6, 17.5) * mm});
            skLineSegment(sketch, "E118.MirrorCS", {"start": v(25, 28) * mm, "end": v(25, 23.95) * mm});
            skLineSegment(sketch, "E119.MirrorCS", {"start": v(0, 25) * mm, "end": v(6, 25) * mm});
            skLineSegment(sketch, "E120.MirrorCS", {"start": v(7, 24) * mm, "end": v(7, 18.5) * mm});
            skLineSegment(sketch, "E121.MirrorCS", {"start": v(0, 27) * mm, "end": v(25, 27) * mm, "construction": true});
            skLineSegment(sketch, "E122.MirrorCS", {"start": v(25, 25) * mm, "end": v(0, 25) * mm, "construction": true});
            skLineSegment(sketch, "E123.MirrorCS", {"start": v(0, 29) * mm, "end": v(24, 29) * mm});
            skPoint(sketch, "E124.MirrorP", {"position": v(25, 23) * mm});
            skPoint(sketch, "E125.MirrorP", {"position": v(25, 29) * mm});
            skArc(sketch, "E126.MirrorCS", {"start": v(17.58, 10.15) * mm, "mid": v(17.37, 18.32) * mm, "end": v(24.1, 22.95) * mm});
            skCircle(sketch, "E127.MirrorC", {"center": v(25, 27) * mm, "radius": 2 * mm, "construction": true});
            skLineSegment(sketch, "E128.MirrorCS", {"start": v(6, 17.5) * mm, "end": v(0, 17.5) * mm});
            skCircle(sketch, "E129.MirrorC", {"center": v(12.25, 19.75) * mm, "radius": 2.1 * mm});
            skPoint(sketch, "E130.MirrorP", {"position": v(7, 17.5) * mm});
            skLineSegment(sketch, "E131.MirrorCS", {"start": v(17.58, 10.15) * mm, "end": v(7.85, 27) * mm, "construction": true});
            skLineSegment(sketch, "E132.MirrorCS", {"start": v(25, 23) * mm, "end": v(0, 23) * mm, "construction": true});
            skPoint(sketch, "E133.MirrorP", {"position": v(7, 25) * mm});
            skCircle(sketch, "E134.MirrorC", {"center": v(12.25, 19.75) * mm, "radius": 5.25 * mm, "construction": true});
            skLineSegment(sketch, "E135.1.0", {"start": v(-23.38, -13.5) * mm, "end": v(-10.88, -35.15) * mm, "construction": true});
            skLineSegment(sketch, "E135.1.1", {"start": v(-34.15, 9.15) * mm, "end": v(-21.65, -12.5) * mm, "construction": true});
            skCircle(sketch, "E135.1.2", {"center": v(-10.98, -20.48) * mm, "radius": 5.25 * mm, "construction": true});
            skCircle(sketch, "E135.1.3", {"center": v(-23.23, 0.73) * mm, "radius": 2.1 * mm});
            skPoint(sketch, "E135.1.4", {"position": v(-11.66, -14.81) * mm});
            skCircle(sketch, "E135.1.5", {"center": v(-23.23, 0.73) * mm, "radius": 5.25 * mm, "construction": true});
            skCircle(sketch, "E135.1.6", {"center": v(-10.88, -35.15) * mm, "radius": 2 * mm, "construction": true});
            skLineSegment(sketch, "E135.1.7", {"start": v(-25.11, -14.5) * mm, "end": v(-37.11, 6.28) * mm});
            skArc(sketch, "E135.1.8", {"start": v(-17.58, 10.15) * mm, "mid": v(-24.55, 5.88) * mm, "end": v(-31.93, 9.4) * mm});
            skLineSegment(sketch, "E135.1.9", {"start": v(-32.42, 10.15) * mm, "end": v(-19.92, -11.5) * mm, "construction": true});
            skArc(sketch, "E135.1.10", {"start": v(0, -20.3) * mm, "mid": v(-7.18, -24.2) * mm, "end": v(-7.83, -32.35) * mm});
            skLineSegment(sketch, "E135.1.11", {"start": v(-18.16, -3.55) * mm, "end": v(-15.16, -8.75) * mm});
            skCircle(sketch, "E135.1.12", {"center": v(-10.98, -20.48) * mm, "radius": 2.1 * mm});
            skPoint(sketch, "E135.1.13", {"position": v(-32.42, 10.15) * mm});
            skPoint(sketch, "E135.1.14", {"position": v(-25.15, -6.44) * mm});
            skLineSegment(sketch, "E135.1.15", {"start": v(-17.58, 10.15) * mm, "end": v(-27.3, -6.7) * mm, "construction": true});
            skLineSegment(sketch, "E135.1.16", {"start": v(-23.38, -13.5) * mm, "end": v(-35.88, 8.15) * mm, "construction": true});
            skCircle(sketch, "E135.1.17", {"center": v(-35.88, 8.15) * mm, "radius": 2 * mm, "construction": true});
            skPoint(sketch, "E135.1.18", {"position": v(-18.15, -18.56) * mm});
            skLineSegment(sketch, "E135.1.19", {"start": v(-7.42, -33.15) * mm, "end": v(-19.92, -11.5) * mm, "construction": true});
            skLineSegment(sketch, "E135.1.20", {"start": v(-9.15, -34.15) * mm, "end": v(-21.65, -12.5) * mm, "construction": true});
            skPoint(sketch, "E135.1.21", {"position": v(-18.66, -2.69) * mm});
            skLineSegment(sketch, "E135.1.22", {"start": v(-24.28, -5.94) * mm, "end": v(-19.52, -3.19) * mm});
            skLineSegment(sketch, "E135.1.23", {"start": v(-12.16, -13.95) * mm, "end": v(-15.16, -8.75) * mm});
            skPoint(sketch, "E135.1.24", {"position": v(-37.61, 7.15) * mm});
            skLineSegment(sketch, "E135.1.25", {"start": v(-25.11, -14.5) * mm, "end": v(-13.11, -35.28) * mm});
            skPoint(sketch, "E135.1.26", {"position": v(-12.61, -36.15) * mm});
            skLineSegment(sketch, "E135.1.27", {"start": v(0, -20.3) * mm, "end": v(-19.46, -20.3) * mm, "construction": true});
            skPoint(sketch, "E135.1.28", {"position": v(-7.42, -33.15) * mm});
            skLineSegment(sketch, "E135.1.29", {"start": v(-17.28, -18.06) * mm, "end": v(-12.52, -15.31) * mm});
            skLineSegment(sketch, "E135.1.30", {"start": v(-21.65, -12.5) * mm, "end": v(-24.65, -7.3) * mm});
            skLineSegment(sketch, "E135.1.31", {"start": v(-36.75, 7.65) * mm, "end": v(-33.24, 9.68) * mm});
            skLineSegment(sketch, "E135.1.32", {"start": v(-11.75, -35.65) * mm, "end": v(-8.24, -33.62) * mm});
            skLineSegment(sketch, "E135.1.33", {"start": v(-21.65, -12.5) * mm, "end": v(-18.65, -17.7) * mm});
            skArc(sketch, "E135.1.34", {"start": v(-19.52, -3.19) * mm, "mid": v(-18.76, -3.09) * mm, "end": v(-18.16, -3.55) * mm});
            skArc(sketch, "E135.1.35", {"start": v(-37.11, 6.28) * mm, "mid": v(-37.21, 7.04) * mm, "end": v(-36.75, 7.65) * mm});
            skArc(sketch, "E135.1.36", {"start": v(-8.24, -33.62) * mm, "mid": v(-7.79, -33.07) * mm, "end": v(-7.83, -32.35) * mm});
            skArc(sketch, "E135.1.37", {"start": v(-24.65, -7.3) * mm, "mid": v(-24.75, -6.55) * mm, "end": v(-24.28, -5.94) * mm});
            skArc(sketch, "E135.1.38", {"start": v(-18.65, -17.7) * mm, "mid": v(-18.04, -18.16) * mm, "end": v(-17.28, -18.06) * mm});
            skArc(sketch, "E135.1.39", {"start": v(-33.24, 9.68) * mm, "mid": v(-32.53, 9.79) * mm, "end": v(-31.93, 9.4) * mm});
            skArc(sketch, "E135.1.40", {"start": v(-13.11, -35.28) * mm, "mid": v(-12.5, -35.75) * mm, "end": v(-11.75, -35.65) * mm});
            skArc(sketch, "E135.1.41", {"start": v(-12.52, -15.31) * mm, "mid": v(-12.06, -14.7) * mm, "end": v(-12.16, -13.95) * mm});
            skLineSegment(sketch, "E135.2.0", {"start": v(23.38, -13.5) * mm, "end": v(35.88, 8.15) * mm, "construction": true});
            skLineSegment(sketch, "E135.2.1", {"start": v(9.15, -34.15) * mm, "end": v(21.65, -12.5) * mm, "construction": true});
            skCircle(sketch, "E135.2.2", {"center": v(23.23, 0.73) * mm, "radius": 5.25 * mm, "construction": true});
            skCircle(sketch, "E135.2.3", {"center": v(10.98, -20.48) * mm, "radius": 2.1 * mm});
            skPoint(sketch, "E135.2.4", {"position": v(18.66, -2.69) * mm});
            skCircle(sketch, "E135.2.5", {"center": v(10.98, -20.48) * mm, "radius": 5.25 * mm, "construction": true});
            skCircle(sketch, "E135.2.6", {"center": v(35.88, 8.15) * mm, "radius": 2 * mm, "construction": true});
            skLineSegment(sketch, "E135.2.7", {"start": v(25.11, -14.5) * mm, "end": v(13.11, -35.28) * mm});
            skArc(sketch, "E135.2.8", {"start": v(0, -20.3) * mm, "mid": v(7.18, -24.2) * mm, "end": v(7.83, -32.35) * mm});
            skLineSegment(sketch, "E135.2.9", {"start": v(7.42, -33.15) * mm, "end": v(19.92, -11.5) * mm, "construction": true});
            skArc(sketch, "E135.2.10", {"start": v(17.58, 10.15) * mm, "mid": v(24.55, 5.88) * mm, "end": v(31.93, 9.4) * mm});
            skLineSegment(sketch, "E135.2.11", {"start": v(12.16, -13.95) * mm, "end": v(15.16, -8.75) * mm});
            skCircle(sketch, "E135.2.12", {"center": v(23.23, 0.73) * mm, "radius": 2.1 * mm});
            skPoint(sketch, "E135.2.13", {"position": v(7.42, -33.15) * mm});
            skPoint(sketch, "E135.2.14", {"position": v(18.15, -18.56) * mm});
            skLineSegment(sketch, "E135.2.15", {"start": v(0, -20.3) * mm, "end": v(19.46, -20.3) * mm, "construction": true});
            skLineSegment(sketch, "E135.2.16", {"start": v(23.38, -13.5) * mm, "end": v(10.88, -35.15) * mm, "construction": true});
            skCircle(sketch, "E135.2.17", {"center": v(10.88, -35.15) * mm, "radius": 2 * mm, "construction": true});
            skPoint(sketch, "E135.2.18", {"position": v(25.15, -6.44) * mm});
            skLineSegment(sketch, "E135.2.19", {"start": v(32.42, 10.15) * mm, "end": v(19.92, -11.5) * mm, "construction": true});
            skLineSegment(sketch, "E135.2.20", {"start": v(34.15, 9.15) * mm, "end": v(21.65, -12.5) * mm, "construction": true});
            skPoint(sketch, "E135.2.21", {"position": v(11.66, -14.81) * mm});
            skLineSegment(sketch, "E135.2.22", {"start": v(17.28, -18.06) * mm, "end": v(12.52, -15.31) * mm});
            skLineSegment(sketch, "E135.2.23", {"start": v(18.16, -3.55) * mm, "end": v(15.16, -8.75) * mm});
            skPoint(sketch, "E135.2.24", {"position": v(12.61, -36.15) * mm});
            skLineSegment(sketch, "E135.2.25", {"start": v(25.11, -14.5) * mm, "end": v(37.11, 6.28) * mm});
            skPoint(sketch, "E135.2.26", {"position": v(37.61, 7.15) * mm});
            skLineSegment(sketch, "E135.2.27", {"start": v(17.58, 10.15) * mm, "end": v(27.3, -6.7) * mm, "construction": true});
            skPoint(sketch, "E135.2.28", {"position": v(32.42, 10.15) * mm});
            skLineSegment(sketch, "E135.2.29", {"start": v(24.28, -5.94) * mm, "end": v(19.52, -3.19) * mm});
            skLineSegment(sketch, "E135.2.30", {"start": v(21.65, -12.5) * mm, "end": v(18.65, -17.7) * mm});
            skLineSegment(sketch, "E135.2.31", {"start": v(11.75, -35.65) * mm, "end": v(8.24, -33.62) * mm});
            skLineSegment(sketch, "E135.2.32", {"start": v(36.75, 7.65) * mm, "end": v(33.24, 9.68) * mm});
            skLineSegment(sketch, "E135.2.33", {"start": v(21.65, -12.5) * mm, "end": v(24.65, -7.3) * mm});
            skArc(sketch, "E135.2.34", {"start": v(12.52, -15.31) * mm, "mid": v(12.06, -14.7) * mm, "end": v(12.16, -13.95) * mm});
            skArc(sketch, "E135.2.35", {"start": v(13.11, -35.28) * mm, "mid": v(12.5, -35.75) * mm, "end": v(11.75, -35.65) * mm});
            skArc(sketch, "E135.2.36", {"start": v(33.24, 9.68) * mm, "mid": v(32.53, 9.79) * mm, "end": v(31.93, 9.4) * mm});
            skArc(sketch, "E135.2.37", {"start": v(18.65, -17.7) * mm, "mid": v(18.04, -18.16) * mm, "end": v(17.28, -18.06) * mm});
            skArc(sketch, "E135.2.38", {"start": v(24.65, -7.3) * mm, "mid": v(24.75, -6.55) * mm, "end": v(24.28, -5.94) * mm});
            skArc(sketch, "E135.2.39", {"start": v(8.24, -33.62) * mm, "mid": v(7.79, -33.07) * mm, "end": v(7.83, -32.35) * mm});
            skArc(sketch, "E135.2.40", {"start": v(37.11, 6.28) * mm, "mid": v(37.21, 7.04) * mm, "end": v(36.75, 7.65) * mm});
            skArc(sketch, "E135.2.41", {"start": v(19.52, -3.19) * mm, "mid": v(18.76, -3.09) * mm, "end": v(18.16, -3.55) * mm});
            skSolve(sketch);
        }
        {
            var Q0;
            Q0=qSketchRegion(id+"F4",true);
            extrude(context, id + "F5", {"entities" : qUnion([Q0]), "oppositeDirection" : true, "depth" : 2 * mm, "offsetDistance" : 25 * mm});
        }
    });
